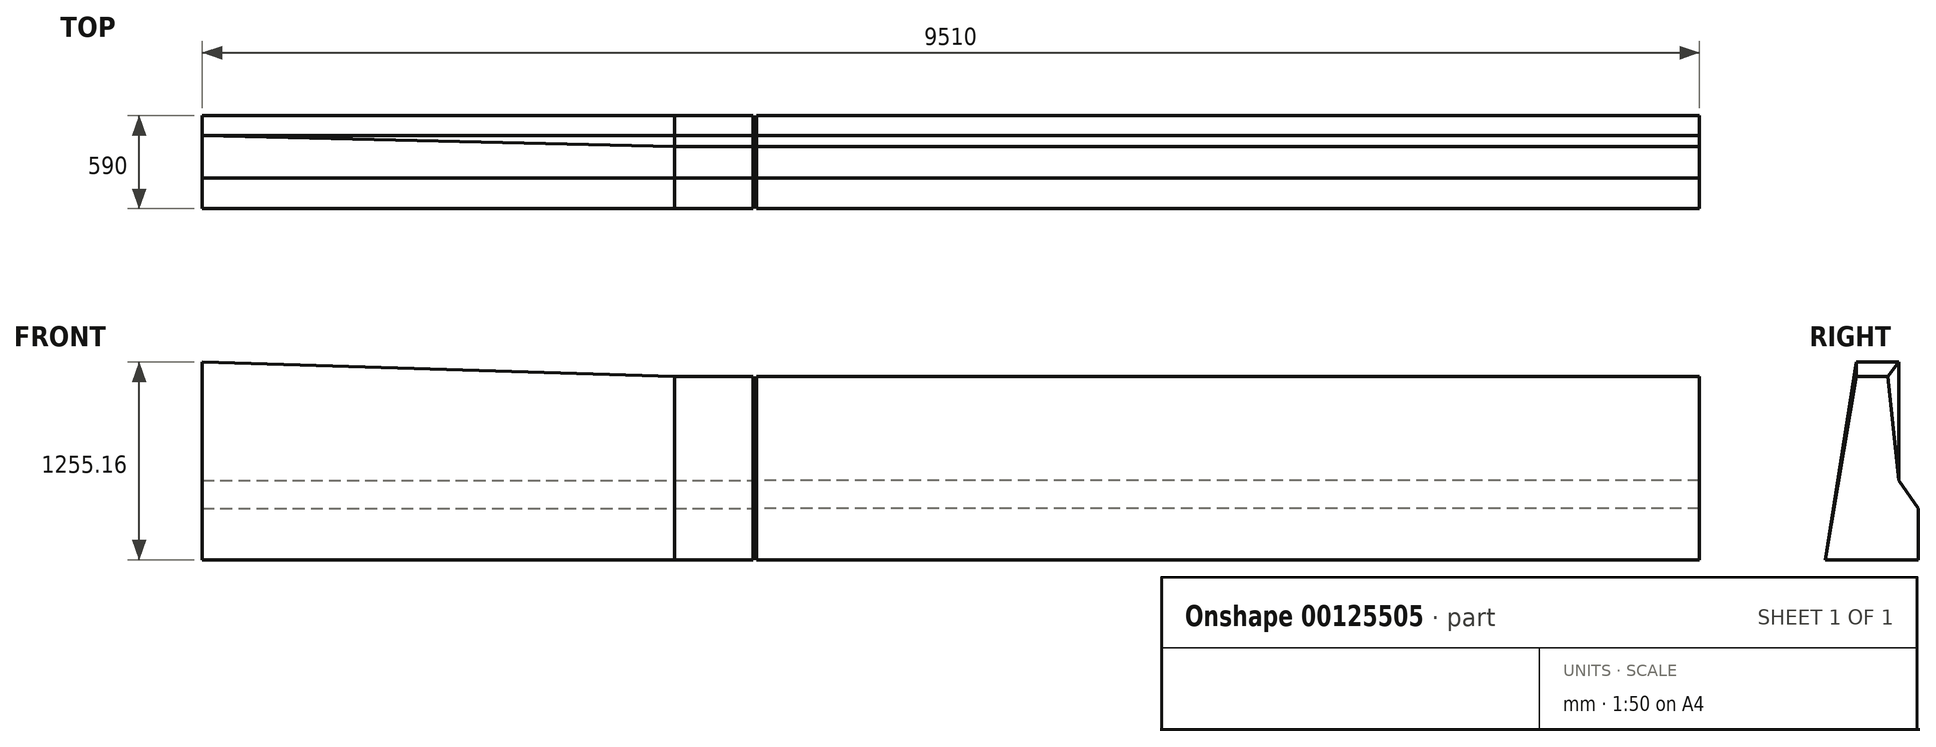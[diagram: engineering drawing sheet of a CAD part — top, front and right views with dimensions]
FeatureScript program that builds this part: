
annotation { "Feature Type Name" : "Feature", "Feature Type Description" : "" }
export const myFeature = defineFeature(function(context is Context, id is Id, definition is map)
    precondition{}
    {
        {
            var Q0;
            Q0=qCreatedBy(makeId("Right.planeOp"),FACE);
            var sketch = newSketch(context, id + "F0", { "sketchPlane" : qUnion([Q0])});
            skLineSegment(sketch, "E0", {"start": v(0, 0) * mm, "end": v(465, 0) * mm});
            skLineSegment(sketch, "E1", {"start": v(465, 0) * mm, "end": v(465, 1255) * mm});
            skLineSegment(sketch, "E2", {"start": v(465, 1255) * mm, "end": v(195, 1255) * mm});
            skLineSegment(sketch, "E3", {"start": v(195, 1255) * mm, "end": v(0, 325) * mm});
            skLineSegment(sketch, "E4", {"start": v(0, 325) * mm, "end": v(0, 0) * mm});
            skSolve(sketch);
        }
        {
            var Q0;
            Q0=makeQuery(id+"F0.imprint","IMPRINT",FACE,{"disambiguationData":[TD([[makeQuery(id+"F0.imprint","IMPRINT",EDGE,{"derivedFrom":sQuery(id+"F0.wireOp",EDGE,"E0")}),1.0]])]});
            cPlane(context, id + "F1", {"entities" : qUnion([Q0]), "cplaneType" : CPlaneType.OFFSET, "offset" : 780 * mm, "width" : 150 * mm, "height" : 150 * mm});
        }
        {
            var Q0;
            Q0=qCreatedBy(id+"F1.planeOp",FACE);
            cPlane(context, id + "F2", {"entities" : qUnion([Q0]), "cplaneType" : CPlaneType.OFFSET, "offset" : 3000 * mm, "width" : 150 * mm, "height" : 150 * mm});
        }
        {
            var Q0;
            Q0=qCreatedBy(id+"F2.planeOp",FACE);
            cPlane(context, id + "F3", {"entities" : qUnion([Q0]), "cplaneType" : CPlaneType.OFFSET, "offset" : 500 * mm, "width" : 150 * mm, "height" : 150 * mm});
        }
        {
            var Q0;
            Q0=qCreatedBy(id+"F3.planeOp",FACE);
            var sketch = newSketch(context, id + "F4", { "sketchPlane" : qUnion([Q0])});
            skLineSegment(sketch, "E5", {"start": v(465, 0) * mm, "end": v(465, 325) * mm});
            skLineSegment(sketch, "E6", {"start": v(465, 325) * mm, "end": v(340, 505) * mm});
            skLineSegment(sketch, "E7", {"start": v(340, 505) * mm, "end": v(270, 1165) * mm});
            skLineSegment(sketch, "E8", {"start": v(270, 1165) * mm, "end": v(70, 1165) * mm});
            skLineSegment(sketch, "E9", {"start": v(70, 1165) * mm, "end": v(-125, 0) * mm});
            skLineSegment(sketch, "E10", {"start": v(465, 0) * mm, "end": v(-125, 0) * mm});
            skSolve(sketch);
        }
        {
            var Q0;
            Q0=qCreatedBy(id+"F2.planeOp",FACE);
            var sketch = newSketch(context, id + "F5", { "sketchPlane" : qUnion([Q0])});
            skLineSegment(sketch, "E11", {"start": v(465, 0) * mm, "end": v(465, 325) * mm});
            skLineSegment(sketch, "E12", {"start": v(465, 325) * mm, "end": v(340, 505) * mm});
            skLineSegment(sketch, "E13", {"start": v(340, 505) * mm, "end": v(270, 1165) * mm});
            skLineSegment(sketch, "E14", {"start": v(270, 1165) * mm, "end": v(70, 1165) * mm});
            skLineSegment(sketch, "E15", {"start": v(70, 1165) * mm, "end": v(-125, 0) * mm});
            skLineSegment(sketch, "E16", {"start": v(465, 0) * mm, "end": v(-125, 0) * mm});
            skLineSegment(sketch, "E17.0", {"start": v(120.8, 1105) * mm, "end": v(-54.12, 60) * mm});
            skLineSegment(sketch, "E17.1", {"start": v(405, 60) * mm, "end": v(405, 306.2) * mm});
            skLineSegment(sketch, "E17.2", {"start": v(405, 306.2) * mm, "end": v(281.95, 483.4) * mm});
            skLineSegment(sketch, "E17.3", {"start": v(281.95, 483.4) * mm, "end": v(216.03, 1105) * mm});
            skLineSegment(sketch, "E17.4", {"start": v(216.03, 1105) * mm, "end": v(120.8, 1105) * mm});
            skSolve(sketch);
        }
        {
            var Q0;
            Q0=makeQuery(id+"F5.imprint","IMPRINT",FACE,{"disambiguationData":[TD([[makeQuery(id+"F5.imprint","IMPRINT",EDGE,{"derivedFrom":sQuery(id+"F5.wireOp",EDGE,"E11")}),1.0]])]});
            var Q1;
            Q1=makeQuery(id+"F4.imprint","IMPRINT",FACE,{"disambiguationData":[TD([[makeQuery(id+"F4.imprint","IMPRINT",EDGE,{"derivedFrom":sQuery(id+"F4.wireOp",EDGE,"E5")}),1.0]])]});
            loft(context, id + "F6", {"sheetProfilesArray" : [{ "sheetProfileEntities" : qUnion([Q0]) }, { "sheetProfileEntities" : qUnion([Q1]) }]});
        }
        {
            var Q0;
            Q0=qCreatedBy(id+"F1.planeOp",FACE);
            var sketch = newSketch(context, id + "F7", { "sketchPlane" : qUnion([Q0])});
            skLineSegment(sketch, "E18", {"start": v(465, 0) * mm, "end": v(465, 325) * mm});
            skLineSegment(sketch, "E19", {"start": v(465, 325) * mm, "end": v(340, 505) * mm});
            skLineSegment(sketch, "E20", {"start": v(340, 505) * mm, "end": v(340, 1255.16) * mm});
            skLineSegment(sketch, "E21", {"start": v(340, 1255.16) * mm, "end": v(70, 1255.16) * mm});
            skLineSegment(sketch, "E22", {"start": v(70, 1255.16) * mm, "end": v(-125, 0) * mm});
            skLineSegment(sketch, "E23", {"start": v(-125, 0) * mm, "end": v(465, 0) * mm});
            skSolve(sketch);
        }
        {
            var Q0;
            Q0=makeQuery(id+"F7.imprint","IMPRINT",FACE,{"disambiguationData":[TD([[makeQuery(id+"F7.imprint","IMPRINT",EDGE,{"derivedFrom":sQuery(id+"F7.wireOp",EDGE,"E18")}),1.0]])]});
            var Q1;
            Q1=makeQuery(id+"F5.imprint","IMPRINT",FACE,{"disambiguationData":[TD([[makeQuery(id+"F5.imprint","IMPRINT",EDGE,{"derivedFrom":sQuery(id+"F5.wireOp",EDGE,"E11")}),1.0]])]});
            loft(context, id + "F8", {"sheetProfilesArray" : [{ "sheetProfileEntities" : qUnion([Q0]) }, { "sheetProfileEntities" : qUnion([Q1]) }]});
        }
        {
            var Q0;
            Q0=qCreatedBy(id+"F3.planeOp",FACE);
            cPlane(context, id + "F9", {"entities" : qUnion([Q0]), "cplaneType" : CPlaneType.OFFSET, "offset" : 20 * mm, "width" : 150 * mm, "height" : 150 * mm});
        }
        {
            var Q0;
            Q0=qCreatedBy(id+"F9.planeOp",FACE);
            var sketch = newSketch(context, id + "F10", { "sketchPlane" : qUnion([Q0])});
            skLineSegment(sketch, "E24", {"start": v(465, 0) * mm, "end": v(465, 325) * mm});
            skLineSegment(sketch, "E25", {"start": v(465, 325) * mm, "end": v(340, 505) * mm});
            skLineSegment(sketch, "E26", {"start": v(340, 505) * mm, "end": v(270, 1165) * mm});
            skLineSegment(sketch, "E27", {"start": v(270, 1165) * mm, "end": v(70, 1165) * mm});
            skLineSegment(sketch, "E28", {"start": v(70, 1165) * mm, "end": v(-125, 0) * mm});
            skLineSegment(sketch, "E29", {"start": v(465, 0) * mm, "end": v(-125, 0) * mm});
            skSolve(sketch);
        }
        {
            var Q0;
            Q0=makeQuery(id+"F10.imprint","IMPRINT",FACE,{"disambiguationData":[TD([[makeQuery(id+"F10.imprint","IMPRINT",EDGE,{"derivedFrom":sQuery(id+"F10.wireOp",EDGE,"E24")}),1.0]])]});
            extrude(context, id + "F11", {"entities" : qUnion([Q0]), "depth" : 5990 * mm});
        }
    });
